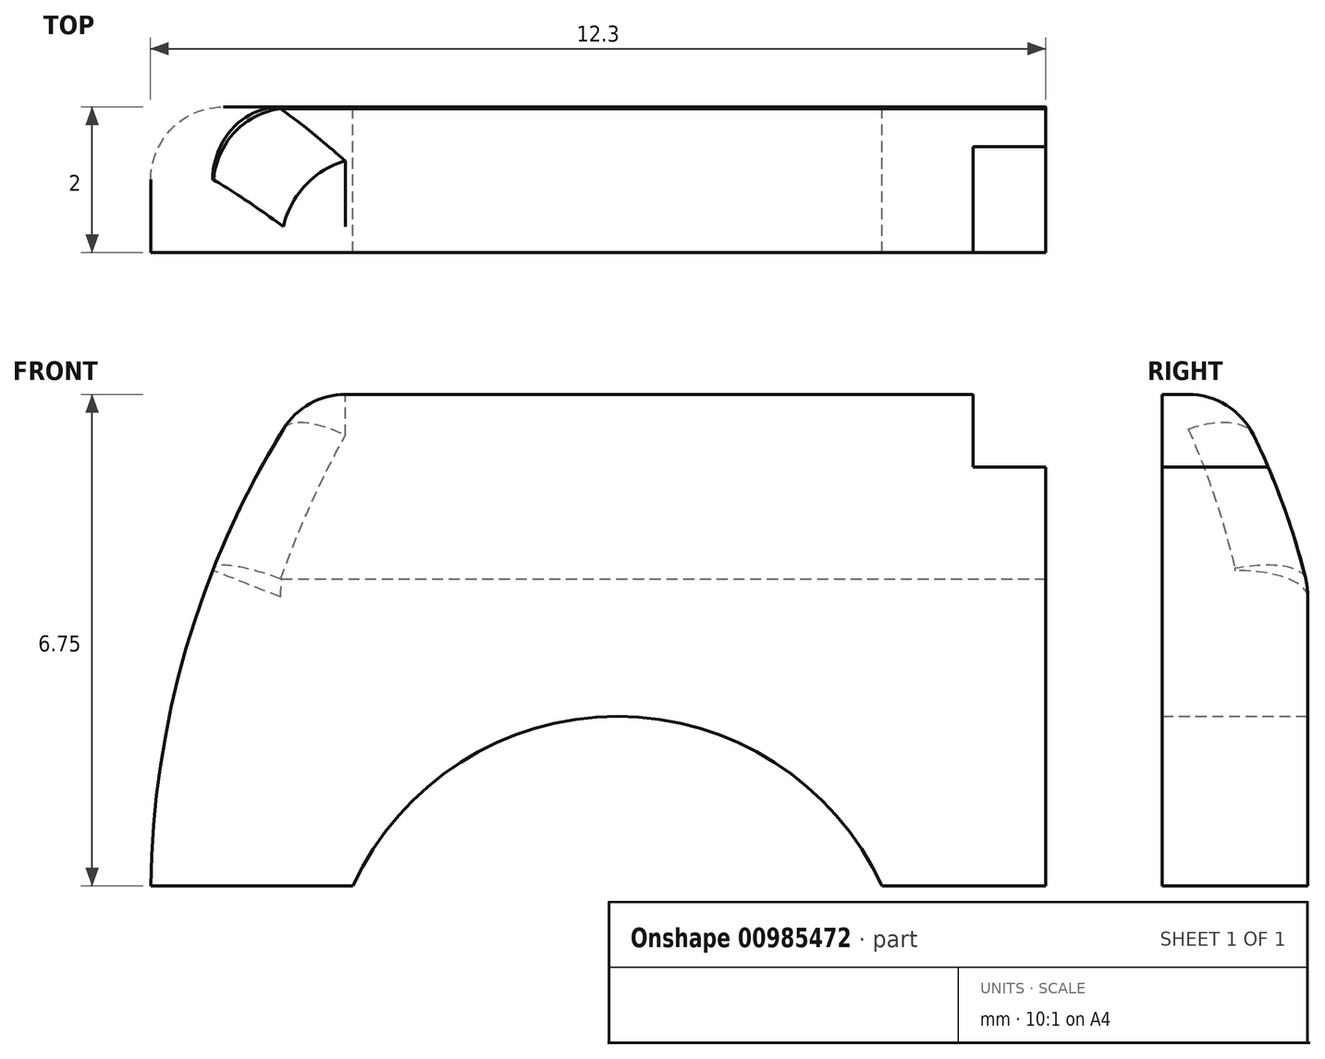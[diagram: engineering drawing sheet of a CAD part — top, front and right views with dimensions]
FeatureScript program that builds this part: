
annotation { "Feature Type Name" : "Feature", "Feature Type Description" : "" }
export const myFeature = defineFeature(function(context is Context, id is Id, definition is map)
    precondition{}
    {
        {
            var Q0;
            Q0=qCreatedBy(makeId("Front.planeOp"),FACE);
            var sketch = newSketch(context, id + "F0", { "sketchPlane" : qUnion([Q0])});
            skLineSegment(sketch, "E0", {"start": v(2.2, -0.4) * mm, "end": v(-0.58, -0.4) * mm});
            skArc(sketch, "E1", {"start": v(1.56, 6.34) * mm, "mid": v(0, 3.12) * mm, "end": v(-0.58, -0.4) * mm});
            skLineSegment(sketch, "E2", {"start": v(1.56, 6.34) * mm, "end": v(11.72, 6.34) * mm});
            skLineSegment(sketch, "E3", {"start": v(11.72, 6.34) * mm, "end": v(11.72, -0.4) * mm});
            skLineSegment(sketch, "E4", {"start": v(11.72, -0.4) * mm, "end": v(9.47, -0.4) * mm});
            skArc(sketch, "E5", {"start": v(9.47, -0.4) * mm, "mid": v(5.84, 1.92) * mm, "end": v(2.2, -0.4) * mm});
            skSolve(sketch);
        }
        {
            var Q0;
            Q0=qSketchRegion(id+"F0",true);
            extrude(context, id + "F1", {"entities" : qUnion([Q0]), "depth" : 2 * mm});
        }
        {
            var Q0;
            Q0=makeQuery(id+"F1.opExtrude","SWEPT_FACE",FACE,{"disambiguationData":[OSD([sQuery(id+"F0.wireOp",EDGE,"E3")])]});
            var sketch = newSketch(context, id + "F2", { "sketchPlane" : qUnion([Q0])});
            skLineSegment(sketch, "E6.MirrorCS", {"start": v(15.38, 6.35) * mm, "end": v(15.38, 6.35) * mm});
            skArc(sketch, "E7.MirrorCS", {"start": v(-0.03, 3.8) * mm, "mid": v(0, 3.68) * mm, "end": v(0, 3.56) * mm});
            skArc(sketch, "E8.MirrorCS", {"start": v(-1.64, 7.27) * mm, "mid": v(-0.67, 5.62) * mm, "end": v(-0.03, 3.8) * mm});
            skPoint(sketch, "E9.MirrorP", {"position": v(-0.05, 3.55) * mm});
            skLineSegment(sketch, "E10.MirrorCS", {"start": v(1, 9.22) * mm, "end": v(-1.64, 7.27) * mm});
            skLineSegment(sketch, "E11.MirrorCS", {"start": v(2.2, 5.65) * mm, "end": v(1, 9.22) * mm});
            skLineSegment(sketch, "E12.MirrorCS", {"start": v(2.2, 5.65) * mm, "end": v(0, 3.56) * mm});
            skSolve(sketch);
        }
        {
            var Q0;
            Q0=qSketchRegion(id+"F2",true);
            extrude(context, id + "F3", {"entities" : qUnion([Q0]), "operationType" : NewBodyOperationType.REMOVE, "endBound" : BoundingType.THROUGH_ALL, "oppositeDirection" : true, "depth" : 25 * mm});
        }
        {
            var Q0;
            Q0=makeQuery(id+"F3.boolean.opBoolean","INTERSECT",EDGE,{"derivedFrom":[makeQuery(id+"F1.opExtrude","SWEPT_FACE",FACE,{"disambiguationData":[OSD([sQuery(id+"F0.wireOp",EDGE,"E2")])]}),makeQuery(id+"F3.opExtrude","SWEPT_FACE",FACE,{"disambiguationData":[OSD([sQuery(id+"F2.wireOp",EDGE,"E8.MirrorCS")])]})]});
            fillet(context, id + "F4", {"entities" : qUnion([Q0]), "radius" : 1 * mm, "tangentPropagation" : true, "allowEdgeOverflow" : false});
        }
        {
            var Q0;
            Q0=makeQuery(id+"F1.opExtrude","SWEPT_EDGE",EDGE,{"disambiguationData":[OSD([sQuery(id+"F0.wireOp",EDGE,"E1"),sQuery(id+"F0.wireOp",EDGE,"E2")])]});
            var Q1;
            Q1=makeQuery(id+"F3.boolean.opBoolean","INTERSECT",EDGE,{"derivedFrom":[makeQuery(id+"F1.opExtrude","SWEPT_FACE",FACE,{"disambiguationData":[OSD([sQuery(id+"F0.wireOp",EDGE,"E1")])]}),makeQuery(id+"F3.opExtrude","SWEPT_FACE",FACE,{"disambiguationData":[OSD([sQuery(id+"F2.wireOp",EDGE,"E8.MirrorCS")])]})]});
            var Q2;
            Q2=makeQuery(id+"F1.opExtrude","CAP_EDGE",EDGE,{"disambiguationData":[OSD([sQuery(id+"F0.wireOp",EDGE,"E1")])],"isStart":true});
            fillet(context, id + "F5", {"entities" : qUnion([Q0, Q1, Q2]), "radius" : 1 * mm, "tangentPropagation" : true, "allowEdgeOverflow" : false});
        }
        {
            var Q0;
            Q0=makeQuery(id+"F1.opExtrude","SWEPT_FACE",FACE,{"disambiguationData":[OSD([sQuery(id+"F0.wireOp",EDGE,"E2")])]});
            var sketch = newSketch(context, id + "F6", { "sketchPlane" : qUnion([Q0])});
            skLineSegment(sketch, "E13.bottom", {"start": v(11.72, -2) * mm, "end": v(10.72, -2) * mm});
            skLineSegment(sketch, "E13.top", {"start": v(11.72, -0.03) * mm, "end": v(10.72, -0.03) * mm});
            skLineSegment(sketch, "E13.left", {"start": v(11.72, -2) * mm, "end": v(11.72, -0.03) * mm});
            skLineSegment(sketch, "E13.right", {"start": v(10.72, -2) * mm, "end": v(10.72, -0.03) * mm});
            skSolve(sketch);
        }
        {
            var Q0;
            Q0=qSketchRegion(id+"F6",true);
            extrude(context, id + "F7", {"entities" : qUnion([Q0]), "operationType" : NewBodyOperationType.REMOVE, "oppositeDirection" : true, "depth" : 1 * mm});
        }
    });
